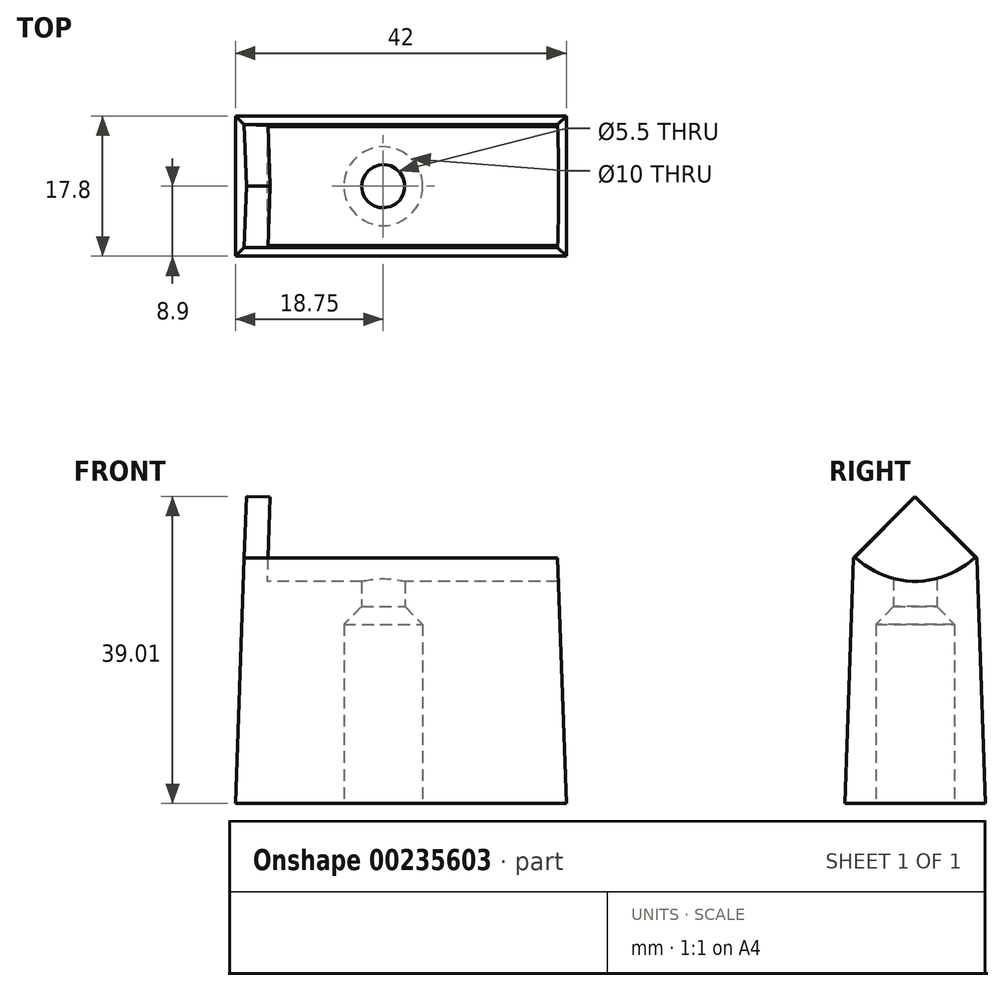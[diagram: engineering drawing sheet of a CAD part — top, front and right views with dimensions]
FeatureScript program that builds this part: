
annotation { "Feature Type Name" : "Feature", "Feature Type Description" : "" }
export const myFeature = defineFeature(function(context is Context, id is Id, definition is map)
    precondition{}
    {
        {
            var Q0;
            Q0=qCreatedBy(makeId("Top.planeOp"),FACE);
            var sketch = newSketch(context, id + "F0", { "sketchPlane" : qUnion([Q0])});
            skLineSegment(sketch, "E0.bottom", {"start": v(21, 8.9) * mm, "end": v(-21, 8.9) * mm});
            skLineSegment(sketch, "E0.top", {"start": v(21, -8.9) * mm, "end": v(-21, -8.9) * mm});
            skLineSegment(sketch, "E0.left", {"start": v(21, 8.9) * mm, "end": v(21, -8.9) * mm});
            skLineSegment(sketch, "E0.right", {"start": v(-21, 8.9) * mm, "end": v(-21, -8.9) * mm});
            skPoint(sketch, "E0.middle", {"position": v(0, 0) * mm});
            skSolve(sketch);
        }
        {
            var Q0;
            Q0=makeQuery(id+"F0.imprint","IMPRINT",FACE,{"disambiguationData":[TD([[makeQuery(id+"F0.imprint","IMPRINT",EDGE,{"derivedFrom":sQuery(id+"F0.wireOp",EDGE,"E0.bottom")}),1.0]])]});
            extrude(context, id + "F1", {"entities" : qUnion([Q0]), "depth" : 31.2 * mm, "hasDraft" : true, "draftAngle" : 2 * degree, "draftPullDirection" : true});
        }
        {
            var Q0;
            Q0=qCreatedBy(makeId("Right.planeOp"),FACE);
            var sketch = newSketch(context, id + "F2", { "sketchPlane" : qUnion([Q0])});
            skCircle(sketch, "E1", {"center": v(0, 39.2) * mm, "radius": 11 * mm});
            skSolve(sketch);
        }
        {
            var Q0;
            Q0=makeQuery(id+"F2.imprint","IMPRINT",FACE,{"disambiguationData":[TD([[makeQuery(id+"F2.imprint","IMPRINT",EDGE,{"derivedFrom":sQuery(id+"F2.wireOp",EDGE,"E1")}),1.0]])]});
            extrude(context, id + "F3", {"entities" : qUnion([Q0]), "operationType" : NewBodyOperationType.REMOVE, "depth" : 50 * mm, "symmetric" : true});
        }
        {
            var Q0;
            Q0=makeQuery(id+"F1.opExtrude","SWEPT_FACE",FACE,{"disambiguationData":[OSD([sQuery(id+"F0.wireOp",EDGE,"E0.right")])]});
            var sketch = newSketch(context, id + "F4", { "sketchPlane" : qUnion([Q0])});
            skLineSegment(sketch, "E2", {"start": v(-7.81, 30.49) * mm, "end": v(0, 38.3) * mm});
            skLineSegment(sketch, "E3", {"start": v(0, 38.3) * mm, "end": v(7.81, 30.49) * mm});
            skSolve(sketch);
        }
        {
            var Q0;
            Q0=makeQuery(id+"F4.imprint","IMPRINT",FACE,{"disambiguationData":[TD([[makeQuery(id+"F4.imprint","IMPRINT",EDGE,{"derivedFrom":sQuery(id+"F4.wireOp",EDGE,"E2")}),-1.0]])]});
            extrude(context, id + "F5", {"entities" : qUnion([Q0]), "operationType" : NewBodyOperationType.ADD, "oppositeDirection" : true, "depth" : 3 * mm});
        }
        {
            var Q0;
            Q0=makeQuery(id+"F1.opExtrude","CAP_FACE",FACE,{"disambiguationData":[OSD([sQuery(id+"F0.wireOp",EDGE,"E0.bottom"),sQuery(id+"F0.wireOp",EDGE,"E0.top"),sQuery(id+"F0.wireOp",EDGE,"E0.left"),sQuery(id+"F0.wireOp",EDGE,"E0.right")])],"isStart":true});
            var sketch = newSketch(context, id + "F6", { "sketchPlane" : qUnion([Q0])});
            skCircle(sketch, "E4", {"center": v(-2.25, 0) * mm, "radius": 2.75 * mm});
            skSolve(sketch);
        }
        {
            var Q0;
            Q0=makeQuery(id+"F6.imprint","IMPRINT",FACE,{"disambiguationData":[TD([[makeQuery(id+"F6.imprint","IMPRINT",EDGE,{"derivedFrom":sQuery(id+"F6.wireOp",EDGE,"E4")}),1.0]])]});
            extrude(context, id + "F7", {"entities" : qUnion([Q0]), "operationType" : NewBodyOperationType.REMOVE, "endBound" : BoundingType.THROUGH_ALL, "oppositeDirection" : true, "depth" : 25 * mm});
        }
        {
            var Q0;
            Q0=makeQuery(id+"F1.opExtrude","CAP_FACE",FACE,{"disambiguationData":[OSD([sQuery(id+"F0.wireOp",EDGE,"E0.bottom"),sQuery(id+"F0.wireOp",EDGE,"E0.top"),sQuery(id+"F0.wireOp",EDGE,"E0.left"),sQuery(id+"F0.wireOp",EDGE,"E0.right")])],"isStart":true});
            var sketch = newSketch(context, id + "F8", { "sketchPlane" : qUnion([Q0])});
            skCircle(sketch, "E5", {"center": v(-2.25, 0) * mm, "radius": 5 * mm});
            skSolve(sketch);
        }
        {
            var Q0;
            Q0=makeQuery(id+"F8.imprint","IMPRINT",FACE,{"disambiguationData":[TD([[makeQuery(id+"F8.imprint","IMPRINT",EDGE,{"derivedFrom":sQuery(id+"F8.wireOp",EDGE,"E5")}),1.0]])]});
            extrude(context, id + "F9", {"entities" : qUnion([Q0]), "operationType" : NewBodyOperationType.REMOVE, "oppositeDirection" : true, "depth" : 25 * mm});
        }
        {
            var Q0;
            Q0=makeQuery(id+"F9.boolean.opBoolean","COPY",EDGE,{"derivedFrom":makeQuery(id+"F9.opExtrude","CAP_EDGE",EDGE,{"disambiguationData":[OSD([sQuery(id+"F8.wireOp",EDGE,"E5")])],"isStart":false})});
            chamfer(context, id + "F10", {"entities" : qUnion([Q0]), "width" : 2.25 * mm, "tangentPropagation" : true});
        }
    });
